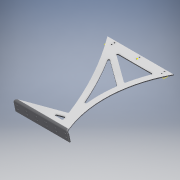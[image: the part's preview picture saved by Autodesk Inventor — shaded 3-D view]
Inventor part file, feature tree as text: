
AUTODESK INVENTOR PART (.ipt)
format: ipt  version: 2016 (Build 200138000, 138)  size: 249,856 bytes
history: native  units: mm
features: sheet_metal_op x4, sketch x4, reference x4, other x2, plane x1, extrude x1, fillet x1, projected_geometry x1
ambient origin geometry x8: Origin, YZ Plane, XZ Plane, XY Plane, X Axis, Y Axis, Z Axis, Center Point
bodies: Solid1 (feature_tree)
feature tree (18):
  plane  "Work Plane1"
  sheet_metal_op  "Face1"
  sketch  "Sketch3"  dims[d11=2000.0mm]
  extrude  "Extrusion1"  Depth=5.0mm
  sheet_metal_op  "Face2"
  sheet_metal_op  "Bend3"
  fillet  "Fillet1"  Radius=500.0mm
  sketch  "Sketch1"  dims[d6=5.0mm d8=50.0mm d9=500.0mm]
  reference  "Reference1"
  other  "Plate1"
  reference  "Reference2"
  sketch  "Sketch4"  dims[d15=30.0mm]
  reference  "Reference4"
  projected_geometry  "Projected Loop2"
  sketch  "Sketch10"  dims[d16=30.0mm d17=30.0mm d18=10.0mm d19=0.0mm d21=3.490659mm d22=30.0mm d23=30.0mm d34=5.0mm d35=5.0mm d36=2.5mm d37=10.0mm d38=5.0mm d39=5.0mm d40=2.5mm d41=10.0mm d42=5.0mm d43=5.0mm d44=5.0mm]
  reference  "Reference17"
  other  "Plate3"
  sheet_metal_op  "Bend2"
